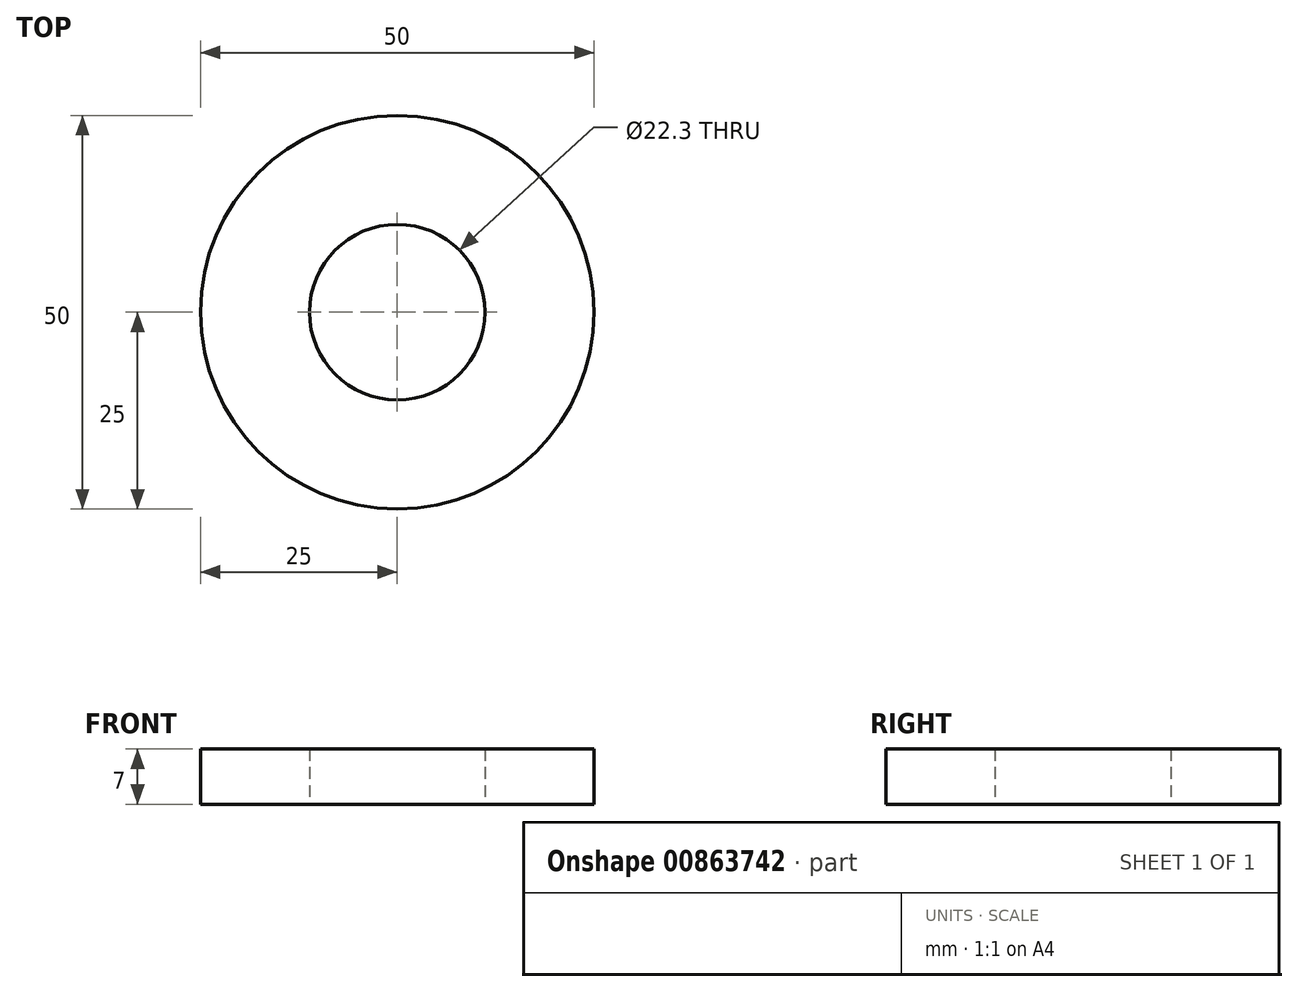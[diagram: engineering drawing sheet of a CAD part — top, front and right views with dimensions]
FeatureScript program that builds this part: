
annotation { "Feature Type Name" : "Feature", "Feature Type Description" : "" }
export const myFeature = defineFeature(function(context is Context, id is Id, definition is map)
    precondition{}
    {
        {
            var Q0;
            Q0=qCreatedBy(makeId("Top.planeOp"),FACE);
            var sketch = newSketch(context, id + "F0", { "sketchPlane" : qUnion([Q0])});
            skCircle(sketch, "E0", {"center": v(0, 0) * mm, "radius": 11.15 * mm});
            skCircle(sketch, "E1", {"center": v(0, 0) * mm, "radius": 25 * mm});
            skSolve(sketch);
        }
        {
            var Q0;
            Q0=makeQuery(id+"F0.imprint","IMPRINT",FACE,{"disambiguationData":[TD([[makeQuery(id+"F0.imprint","IMPRINT",EDGE,{"derivedFrom":sQuery(id+"F0.wireOp",EDGE,"E0")}),-1.0]])]});
            extrude(context, id + "F1", {"entities" : qUnion([Q0]), "depth" : 7 * mm, "offsetDistance" : 25 * mm});
        }
    });
